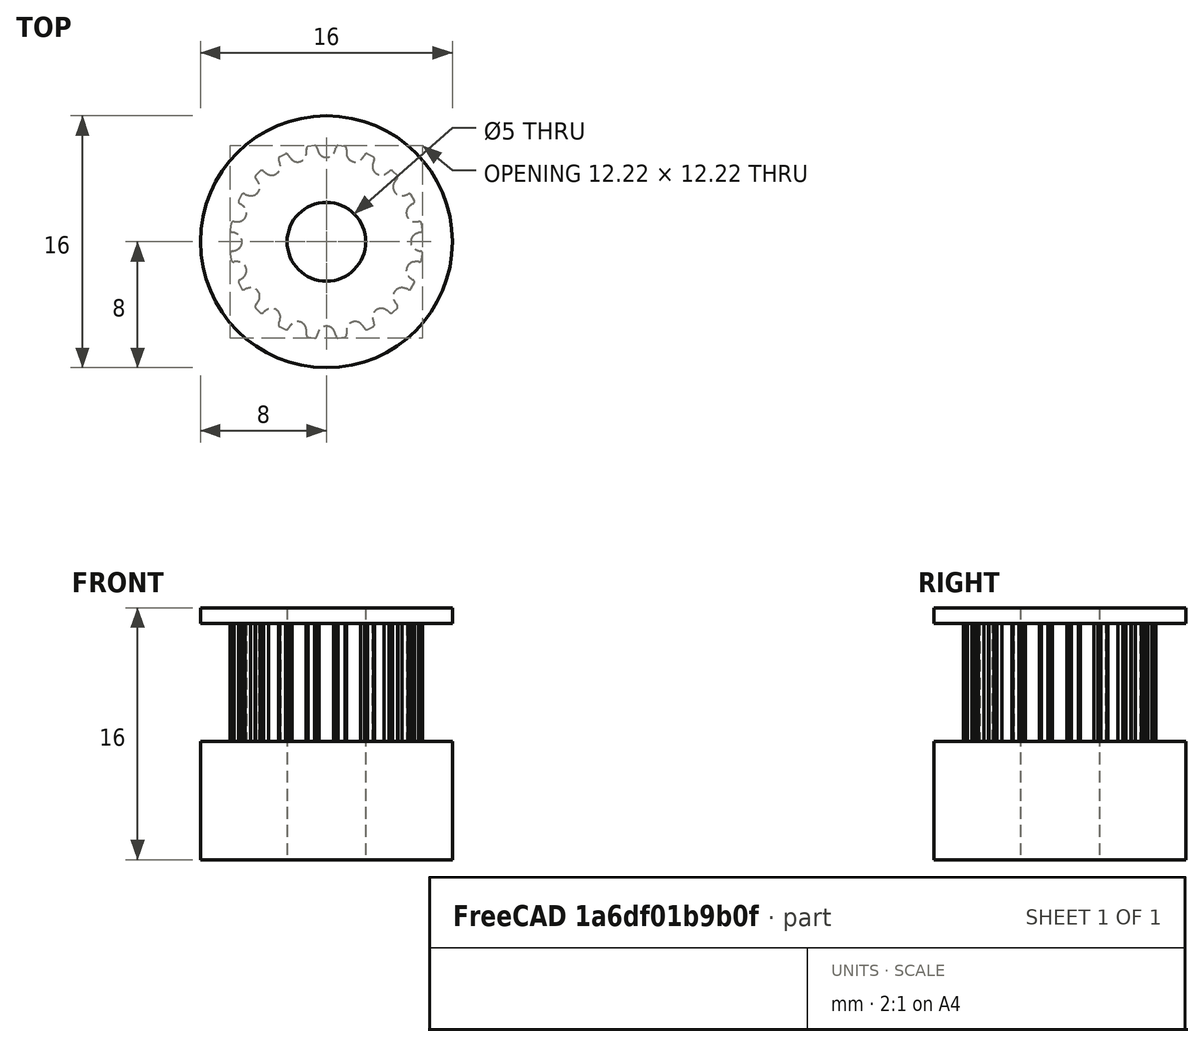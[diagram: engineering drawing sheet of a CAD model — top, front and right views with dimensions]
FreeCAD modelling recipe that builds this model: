
FCSTD DOCUMENT  (FreeCAD 1.0R39319 (Git))
Label: GT2_20
License: All rights reserved
LicenseURL: https://en.wikipedia.org/wiki/All_rights_reserved
objects: Sketcher::SketchObject×3, PartDesign::Pad×3, PartDesign::Body×1
note: 16 computed .brp shape members not serialized (recipe doc carries the construction recipe); baked Part::Feature solids carry a one-line shape summary decoded from their .brp

FEATURE [Sketcher::SketchObject] SketchGear
  ArcFitTolerance = 1e-06
  FullyConstrained = false
  MakeInternals = false
  MapMode = 5
  Placement = pos=(0,0,7.5) rot=(0,0,1;0rad)
  sketch-geometry (121):
    g0: ArcOfCircle CenterX=5.9622 CenterY=-0.75 CenterZ=0 NormalX=0 NormalY=0 NormalZ=1 AngleXU=8.1e-15 Radius=0.15 StartAngle=0 EndAngle=1.5708
    g1: ArcOfCircle CenterX=6.30816 CenterY=0.82798 CenterZ=0 NormalX=0 NormalY=0 NormalZ=-1 AngleXU=-1.3331 Radius=1.46929 StartAngle=0 EndAngle=0.255762
    g2: ArcOfCircle CenterX=5.92156 CenterY=0 CenterZ=0 NormalX=0 NormalY=0 NormalZ=-1 AngleXU=-0.984764 Radius=0.559359 StartAngle=0 EndAngle=1.96953
    g3: ArcOfCircle CenterX=6.30816 CenterY=-0.82798 CenterZ=0 NormalX=0 NormalY=0 NormalZ=-1 AngleXU=1.07734 Radius=1.46929 StartAngle=0 EndAngle=0.255762
    g4: ArcOfCircle CenterX=5.9622 CenterY=0.75 CenterZ=0 NormalX=0 NormalY=0 NormalZ=1 AngleXU=-1.5708 Radius=0.15 StartAngle=0 EndAngle=1.5708
    g5: LineSegment StartX=6.1122 StartY=0.75 StartZ=0 EndX=6.04481 EndY=1.17548 EndZ=0
    g6: ArcOfCircle CenterX=5.90215 CenterY=1.12913 CenterZ=0 NormalX=0 NormalY=0 NormalZ=1 AngleXU=0.314159 Radius=0.15 StartAngle=0 EndAngle=1.5708
    g7: ArcOfCircle CenterX=5.74356 CenterY=2.73679 CenterZ=0 NormalX=0 NormalY=0 NormalZ=-1 AngleXU=-1.64726 Radius=1.46929 StartAngle=0 EndAngle=0.255762
    g8: ArcOfCircle CenterX=5.63174 CenterY=1.82986 CenterZ=0 NormalX=0 NormalY=0 NormalZ=-1 AngleXU=-1.29892 Radius=0.559359 StartAngle=0 EndAngle=1.96953
    g9: ArcOfCircle CenterX=6.25528 CenterY=1.16187 CenterZ=0 NormalX=0 NormalY=0 NormalZ=-1 AngleXU=0.763178 Radius=1.46929 StartAngle=0 EndAngle=0.255762
    g10: ArcOfCircle CenterX=5.43862 CenterY=2.55571 CenterZ=0 NormalX=0 NormalY=0 NormalZ=1 AngleXU=-1.25664 Radius=0.15 StartAngle=0 EndAngle=1.5708
    g11: LineSegment StartX=5.58128 StartY=2.60207 StartZ=0 EndX=5.38571 EndY=2.9859 EndZ=0
    g12: ArcOfCircle CenterX=5.26436 CenterY=2.89773 CenterZ=0 NormalX=0 NormalY=0 NormalZ=1 AngleXU=0.628319 Radius=0.15 StartAngle=0 EndAngle=1.5708
    g13: ArcOfCircle CenterX=4.61674 CenterY=4.3777 CenterZ=0 NormalX=0 NormalY=0 NormalZ=-1 AngleXU=-1.96142 Radius=1.46929 StartAngle=0 EndAngle=0.255762
    g14: ArcOfCircle CenterX=4.79064 CenterY=3.4806 CenterZ=0 NormalX=0 NormalY=0 NormalZ=-1 AngleXU=-1.61308 Radius=0.559359 StartAngle=0 EndAngle=1.96953
    g15: ArcOfCircle CenterX=5.59009 CenterY=3.038 CenterZ=0 NormalX=0 NormalY=0 NormalZ=-1 AngleXU=0.449019 Radius=1.46929 StartAngle=0 EndAngle=0.255762
    g16: ArcOfCircle CenterX=4.38268 CenterY=4.11125 CenterZ=0 NormalX=0 NormalY=0 NormalZ=1 AngleXU=-0.942478 Radius=0.15 StartAngle=0 EndAngle=1.5708
    g17: LineSegment StartX=4.50403 StartY=4.19942 StartZ=0 EndX=4.19942 EndY=4.50403 EndZ=0
    g18: ArcOfCircle CenterX=4.11125 CenterY=4.38268 CenterZ=0 NormalX=0 NormalY=0 NormalZ=1 AngleXU=0.942478 Radius=0.15 StartAngle=0 EndAngle=1.5708
    g19: ArcOfCircle CenterX=3.038 CenterY=5.59009 CenterZ=0 NormalX=0 NormalY=0 NormalZ=-1 AngleXU=-2.27558 Radius=1.46929 StartAngle=0 EndAngle=0.255762
    g20: ArcOfCircle CenterX=3.4806 CenterY=4.79064 CenterZ=0 NormalX=0 NormalY=0 NormalZ=-1 AngleXU=-1.92724 Radius=0.559359 StartAngle=0 EndAngle=1.96953
    g21: ArcOfCircle CenterX=4.3777 CenterY=4.61674 CenterZ=0 NormalX=0 NormalY=0 NormalZ=-1 AngleXU=0.13486 Radius=1.46929 StartAngle=0 EndAngle=0.255762
    g22: ArcOfCircle CenterX=2.89773 CenterY=5.26436 CenterZ=0 NormalX=0 NormalY=0 NormalZ=1 AngleXU=-0.628319 Radius=0.15 StartAngle=0 EndAngle=1.5708
    g23: LineSegment StartX=2.9859 StartY=5.38571 StartZ=0 EndX=2.60207 EndY=5.58128 EndZ=0
    g24: ArcOfCircle CenterX=2.55571 CenterY=5.43862 CenterZ=0 NormalX=0 NormalY=0 NormalZ=1 AngleXU=1.25664 Radius=0.15 StartAngle=0 EndAngle=1.5708
    g25: ArcOfCircle CenterX=1.16187 CenterY=6.25528 CenterZ=0 NormalX=0 NormalY=0 NormalZ=-1 AngleXU=-2.58974 Radius=1.46929 StartAngle=0 EndAngle=0.255762
    g26: ArcOfCircle CenterX=1.82986 CenterY=5.63174 CenterZ=0 NormalX=0 NormalY=0 NormalZ=-1 AngleXU=-2.2414 Radius=0.559359 StartAngle=0 EndAngle=1.96953
    g27: ArcOfCircle CenterX=2.73679 CenterY=5.74356 CenterZ=0 NormalX=0 NormalY=0 NormalZ=-1 AngleXU=-0.1793 Radius=1.46929 StartAngle=0 EndAngle=0.255762
    g28: ArcOfCircle CenterX=1.12913 CenterY=5.90215 CenterZ=0 NormalX=0 NormalY=0 NormalZ=1 AngleXU=-0.314159 Radius=0.15 StartAngle=0 EndAngle=1.5708
    g29: LineSegment StartX=1.17548 StartY=6.04481 StartZ=0 EndX=0.75 EndY=6.1122 EndZ=0
    g30: ArcOfCircle CenterX=0.75 CenterY=5.9622 CenterZ=0 NormalX=0 NormalY=0 NormalZ=1 AngleXU=1.5708 Radius=0.15 StartAngle=0 EndAngle=1.5708
    g31: ArcOfCircle CenterX=-0.82798 CenterY=6.30816 CenterZ=0 NormalX=0 NormalY=0 NormalZ=-1 AngleXU=-2.9039 Radius=1.46929 StartAngle=0 EndAngle=0.255762
    g32: ArcOfCircle CenterX=4e-16 CenterY=5.92156 CenterZ=0 NormalX=0 NormalY=0 NormalZ=-1 AngleXU=-2.55556 Radius=0.559359 StartAngle=0 EndAngle=1.96953
    g33: ArcOfCircle CenterX=0.82798 CenterY=6.30816 CenterZ=0 NormalX=0 NormalY=0 NormalZ=-1 AngleXU=-0.493459 Radius=1.46929 StartAngle=0 EndAngle=0.255762
    g34: ArcOfCircle CenterX=-0.75 CenterY=5.9622 CenterZ=0 NormalX=0 NormalY=0 NormalZ=1 AngleXU=5.9e-15 Radius=0.15 StartAngle=0 EndAngle=1.5708
    g35: LineSegment StartX=-0.75 StartY=6.1122 StartZ=0 EndX=-1.17548 EndY=6.04481 EndZ=0
    g36: ArcOfCircle CenterX=-1.12913 CenterY=5.90215 CenterZ=0 NormalX=0 NormalY=0 NormalZ=1 AngleXU=1.88496 Radius=0.15 StartAngle=0 EndAngle=1.5708
    g37: ArcOfCircle CenterX=-2.73679 CenterY=5.74356 CenterZ=0 NormalX=0 NormalY=0 NormalZ=-1 AngleXU=3.06513 Radius=1.46929 StartAngle=0 EndAngle=0.255762
    g38: ArcOfCircle CenterX=-1.82986 CenterY=5.63174 CenterZ=0 NormalX=0 NormalY=0 NormalZ=-1 AngleXU=-2.86972 Radius=0.559359 StartAngle=0 EndAngle=1.96953
    g39: ArcOfCircle CenterX=-1.16187 CenterY=6.25528 CenterZ=0 NormalX=0 NormalY=0 NormalZ=-1 AngleXU=-0.807618 Radius=1.46929 StartAngle=0 EndAngle=0.255762
    g40: ArcOfCircle CenterX=-2.55571 CenterY=5.43862 CenterZ=0 NormalX=0 NormalY=0 NormalZ=1 AngleXU=0.314159 Radius=0.15 StartAngle=0 EndAngle=1.5708
    g41: LineSegment StartX=-2.60207 StartY=5.58128 StartZ=0 EndX=-2.9859 EndY=5.38571 EndZ=0
    g42: ArcOfCircle CenterX=-2.89773 CenterY=5.26436 CenterZ=0 NormalX=0 NormalY=0 NormalZ=1 AngleXU=2.19911 Radius=0.15 StartAngle=0 EndAngle=1.5708
    g43: ArcOfCircle CenterX=-4.3777 CenterY=4.61674 CenterZ=0 NormalX=0 NormalY=0 NormalZ=-1 AngleXU=2.75097 Radius=1.46929 StartAngle=0 EndAngle=0.255762
    g44: ArcOfCircle CenterX=-3.4806 CenterY=4.79064 CenterZ=0 NormalX=0 NormalY=0 NormalZ=-1 AngleXU=3.09931 Radius=0.559359 StartAngle=0 EndAngle=1.96953
    g45: ArcOfCircle CenterX=-3.038 CenterY=5.59009 CenterZ=0 NormalX=0 NormalY=0 NormalZ=-1 AngleXU=-1.12178 Radius=1.46929 StartAngle=0 EndAngle=0.255762
    g46: ArcOfCircle CenterX=-4.11125 CenterY=4.38268 CenterZ=0 NormalX=0 NormalY=0 NormalZ=1 AngleXU=0.628319 Radius=0.15 StartAngle=0 EndAngle=1.5708
    g47: LineSegment StartX=-4.19942 StartY=4.50403 StartZ=0 EndX=-4.50403 EndY=4.19942 EndZ=0
    g48: ArcOfCircle CenterX=-4.38268 CenterY=4.11125 CenterZ=0 NormalX=0 NormalY=0 NormalZ=1 AngleXU=2.51327 Radius=0.15 StartAngle=0 EndAngle=1.5708
    g49: ArcOfCircle CenterX=-5.59009 CenterY=3.038 CenterZ=0 NormalX=0 NormalY=0 NormalZ=-1 AngleXU=2.43681 Radius=1.46929 StartAngle=0 EndAngle=0.255762
    g50: ArcOfCircle CenterX=-4.79064 CenterY=3.4806 CenterZ=0 NormalX=0 NormalY=0 NormalZ=-1 AngleXU=2.78515 Radius=0.559359 StartAngle=0 EndAngle=1.96953
    g51: ArcOfCircle CenterX=-4.61674 CenterY=4.3777 CenterZ=0 NormalX=0 NormalY=0 NormalZ=-1 AngleXU=-1.43594 Radius=1.46929 StartAngle=0 EndAngle=0.255762
    g52: ArcOfCircle CenterX=-5.26436 CenterY=2.89773 CenterZ=0 NormalX=0 NormalY=0 NormalZ=1 AngleXU=0.942478 Radius=0.15 StartAngle=0 EndAngle=1.5708
    g53: LineSegment StartX=-5.38571 StartY=2.9859 StartZ=0 EndX=-5.58128 EndY=2.60207 EndZ=0
    g54: ArcOfCircle CenterX=-5.43862 CenterY=2.55571 CenterZ=0 NormalX=0 NormalY=0 NormalZ=1 AngleXU=2.82743 Radius=0.15 StartAngle=0 EndAngle=1.5708
    g55: ArcOfCircle CenterX=-6.25528 CenterY=1.16187 CenterZ=0 NormalX=0 NormalY=0 NormalZ=-1 AngleXU=2.12265 Radius=1.46929 StartAngle=0 EndAngle=0.255762
    g56: ArcOfCircle CenterX=-5.63174 CenterY=1.82986 CenterZ=0 NormalX=0 NormalY=0 NormalZ=-1 AngleXU=2.47099 Radius=0.559359 StartAngle=0 EndAngle=1.96953
    g57: ArcOfCircle CenterX=-5.74356 CenterY=2.73679 CenterZ=0 NormalX=0 NormalY=0 NormalZ=-1 AngleXU=-1.7501 Radius=1.46929 StartAngle=0 EndAngle=0.255762
    g58: ArcOfCircle CenterX=-5.90215 CenterY=1.12913 CenterZ=0 NormalX=0 NormalY=0 NormalZ=1 AngleXU=1.25664 Radius=0.15 StartAngle=0 EndAngle=1.5708
    g59: LineSegment StartX=-6.04481 StartY=1.17548 StartZ=0 EndX=-6.1122 EndY=0.75 EndZ=0
    g60: ArcOfCircle CenterX=-5.9622 CenterY=0.75 CenterZ=0 NormalX=0 NormalY=0 NormalZ=1 AngleXU=-3.14159 Radius=0.15 StartAngle=0 EndAngle=1.5708
    g61: ArcOfCircle CenterX=-6.30816 CenterY=-0.82798 CenterZ=0 NormalX=0 NormalY=0 NormalZ=-1 AngleXU=1.80849 Radius=1.46929 StartAngle=0 EndAngle=0.255762
    g62: ArcOfCircle CenterX=-5.92156 CenterY=9e-16 CenterZ=0 NormalX=0 NormalY=0 NormalZ=-1 AngleXU=2.15683 Radius=0.559359 StartAngle=0 EndAngle=1.96953
    g63: ArcOfCircle CenterX=-6.30816 CenterY=0.82798 CenterZ=0 NormalX=0 NormalY=0 NormalZ=-1 AngleXU=-2.06426 Radius=1.46929 StartAngle=0 EndAngle=0.255762
    g64: ArcOfCircle CenterX=-5.9622 CenterY=-0.75 CenterZ=0 NormalX=0 NormalY=0 NormalZ=1 AngleXU=1.5708 Radius=0.15 StartAngle=0 EndAngle=1.5708
    g65: LineSegment StartX=-6.1122 StartY=-0.75 StartZ=0 EndX=-6.04481 EndY=-1.17548 EndZ=0
    g66: ArcOfCircle CenterX=-5.90215 CenterY=-1.12913 CenterZ=0 NormalX=0 NormalY=0 NormalZ=1 AngleXU=-2.82743 Radius=0.15 StartAngle=0 EndAngle=1.5708
    g67: ArcOfCircle CenterX=-5.74356 CenterY=-2.73679 CenterZ=0 NormalX=0 NormalY=0 NormalZ=-1 AngleXU=1.49433 Radius=1.46929 StartAngle=0 EndAngle=0.255762
    g68: ArcOfCircle CenterX=-5.63174 CenterY=-1.82986 CenterZ=0 NormalX=0 NormalY=0 NormalZ=-1 AngleXU=1.84267 Radius=0.559359 StartAngle=0 EndAngle=1.96953
    g69: ArcOfCircle CenterX=-6.25528 CenterY=-1.16187 CenterZ=0 NormalX=0 NormalY=0 NormalZ=-1 AngleXU=-2.37841 Radius=1.46929 StartAngle=0 EndAngle=0.255762
    g70: ArcOfCircle CenterX=-5.43862 CenterY=-2.55571 CenterZ=0 NormalX=0 NormalY=0 NormalZ=1 AngleXU=1.88496 Radius=0.15 StartAngle=0 EndAngle=1.5708
    g71: LineSegment StartX=-5.58128 StartY=-2.60207 StartZ=0 EndX=-5.38571 EndY=-2.9859 EndZ=0
    g72: ArcOfCircle CenterX=-5.26436 CenterY=-2.89773 CenterZ=0 NormalX=0 NormalY=0 NormalZ=1 AngleXU=-2.51327 Radius=0.15 StartAngle=0 EndAngle=1.5708
    g73: ArcOfCircle CenterX=-4.61674 CenterY=-4.3777 CenterZ=0 NormalX=0 NormalY=0 NormalZ=-1 AngleXU=1.18017 Radius=1.46929 StartAngle=0 EndAngle=0.255762
    g74: ArcOfCircle CenterX=-4.79064 CenterY=-3.4806 CenterZ=0 NormalX=0 NormalY=0 NormalZ=-1 AngleXU=1.52851 Radius=0.559359 StartAngle=0 EndAngle=1.96953
    g75: ArcOfCircle CenterX=-5.59009 CenterY=-3.038 CenterZ=0 NormalX=0 NormalY=0 NormalZ=-1 AngleXU=-2.69257 Radius=1.46929 StartAngle=0 EndAngle=0.255762
    g76: ArcOfCircle CenterX=-4.38268 CenterY=-4.11125 CenterZ=0 NormalX=0 NormalY=0 NormalZ=1 AngleXU=2.19911 Radius=0.15 StartAngle=0 EndAngle=1.5708
    g77: LineSegment StartX=-4.50403 StartY=-4.19942 StartZ=0 EndX=-4.19942 EndY=-4.50403 EndZ=0
    g78: ArcOfCircle CenterX=-4.11125 CenterY=-4.38268 CenterZ=0 NormalX=0 NormalY=0 NormalZ=1 AngleXU=-2.19911 Radius=0.15 StartAngle=0 EndAngle=1.5708
    g79: ArcOfCircle CenterX=-3.038 CenterY=-5.59009 CenterZ=0 NormalX=0 NormalY=0 NormalZ=-1 AngleXU=0.866016 Radius=1.46929 StartAngle=0 EndAngle=0.255762
    g80: ArcOfCircle CenterX=-3.4806 CenterY=-4.79064 CenterZ=0 NormalX=0 NormalY=0 NormalZ=-1 AngleXU=1.21435 Radius=0.559359 StartAngle=0 EndAngle=1.96953
    g81: ArcOfCircle CenterX=-4.3777 CenterY=-4.61674 CenterZ=0 NormalX=0 NormalY=0 NormalZ=-1 AngleXU=-3.00673 Radius=1.46929 StartAngle=0 EndAngle=0.255762
    g82: ArcOfCircle CenterX=-2.89773 CenterY=-5.26436 CenterZ=0 NormalX=0 NormalY=0 NormalZ=1 AngleXU=2.51327 Radius=0.15 StartAngle=0 EndAngle=1.5708
    g83: LineSegment StartX=-2.9859 StartY=-5.38571 StartZ=0 EndX=-2.60207 EndY=-5.58128 EndZ=0
    g84: ArcOfCircle CenterX=-2.55571 CenterY=-5.43862 CenterZ=0 NormalX=0 NormalY=0 NormalZ=1 AngleXU=-1.88496 Radius=0.15 StartAngle=0 EndAngle=1.5708
    g85: ArcOfCircle CenterX=-1.16187 CenterY=-6.25528 CenterZ=0 NormalX=0 NormalY=0 NormalZ=-1 AngleXU=0.551856 Radius=1.46929 StartAngle=0 EndAngle=0.255762
    g86: ArcOfCircle CenterX=-1.82986 CenterY=-5.63174 CenterZ=0 NormalX=0 NormalY=0 NormalZ=-1 AngleXU=0.900192 Radius=0.559359 StartAngle=0 EndAngle=1.96953
    g87: ArcOfCircle CenterX=-2.73679 CenterY=-5.74356 CenterZ=0 NormalX=0 NormalY=0 NormalZ=-1 AngleXU=2.96229 Radius=1.46929 StartAngle=0 EndAngle=0.255762
    g88: ArcOfCircle CenterX=-1.12913 CenterY=-5.90215 CenterZ=0 NormalX=0 NormalY=0 NormalZ=1 AngleXU=2.82743 Radius=0.15 StartAngle=0 EndAngle=1.5708
    g89: LineSegment StartX=-1.17548 StartY=-6.04481 StartZ=0 EndX=-0.75 EndY=-6.1122 EndZ=0
    g90: ArcOfCircle CenterX=-0.75 CenterY=-5.9622 CenterZ=0 NormalX=0 NormalY=0 NormalZ=1 AngleXU=-1.5708 Radius=0.15 StartAngle=0 EndAngle=1.5708
    g91: ArcOfCircle CenterX=0.82798 CenterY=-6.30816 CenterZ=0 NormalX=0 NormalY=0 NormalZ=-1 AngleXU=0.237697 Radius=1.46929 StartAngle=0 EndAngle=0.255762
    g92: ArcOfCircle CenterX=-9e-16 CenterY=-5.92156 CenterZ=0 NormalX=0 NormalY=0 NormalZ=-1 AngleXU=0.586033 Radius=0.559359 StartAngle=0 EndAngle=1.96953
    g93: ArcOfCircle CenterX=-0.82798 CenterY=-6.30816 CenterZ=0 NormalX=0 NormalY=0 NormalZ=-1 AngleXU=2.64813 Radius=1.46929 StartAngle=0 EndAngle=0.255762
    g94: ArcOfCircle CenterX=0.75 CenterY=-5.9622 CenterZ=0 NormalX=0 NormalY=0 NormalZ=1 AngleXU=-3.14159 Radius=0.15 StartAngle=0 EndAngle=1.5708
    g95: LineSegment StartX=0.75 StartY=-6.1122 StartZ=0 EndX=1.17548 EndY=-6.04481 EndZ=0
    g96: ArcOfCircle CenterX=1.12913 CenterY=-5.90215 CenterZ=0 NormalX=0 NormalY=0 NormalZ=1 AngleXU=-1.25664 Radius=0.15 StartAngle=0 EndAngle=1.5708
    g97: ArcOfCircle CenterX=2.73679 CenterY=-5.74356 CenterZ=0 NormalX=0 NormalY=0 NormalZ=-1 AngleXU=-0.0764622 Radius=1.46929 StartAngle=0 EndAngle=0.255762
    g98: ArcOfCircle CenterX=1.82986 CenterY=-5.63174 CenterZ=0 NormalX=0 NormalY=0 NormalZ=-1 AngleXU=0.271874 Radius=0.559359 StartAngle=0 EndAngle=1.96953
    g99: ArcOfCircle CenterX=1.16187 CenterY=-6.25528 CenterZ=0 NormalX=0 NormalY=0 NormalZ=-1 AngleXU=2.33397 Radius=1.46929 StartAngle=0 EndAngle=0.255762
    g100: ArcOfCircle CenterX=2.55571 CenterY=-5.43862 CenterZ=0 NormalX=0 NormalY=0 NormalZ=1 AngleXU=-2.82743 Radius=0.15 StartAngle=0 EndAngle=1.5708
    g101: LineSegment StartX=2.60207 StartY=-5.58128 StartZ=0 EndX=2.9859 EndY=-5.38571 EndZ=0
    g102: ArcOfCircle CenterX=2.89773 CenterY=-5.26436 CenterZ=0 NormalX=0 NormalY=0 NormalZ=1 AngleXU=-0.942478 Radius=0.15 StartAngle=0 EndAngle=1.5708
    g103: ArcOfCircle CenterX=4.3777 CenterY=-4.61674 CenterZ=0 NormalX=0 NormalY=0 NormalZ=-1 AngleXU=-0.390621 Radius=1.46929 StartAngle=0 EndAngle=0.255762
    g104: ArcOfCircle CenterX=3.4806 CenterY=-4.79064 CenterZ=0 NormalX=0 NormalY=0 NormalZ=-1 AngleXU=-0.0422858 Radius=0.559359 StartAngle=0 EndAngle=1.96953
    g105: ArcOfCircle CenterX=3.038 CenterY=-5.59009 CenterZ=0 NormalX=0 NormalY=0 NormalZ=-1 AngleXU=2.01982 Radius=1.46929 StartAngle=0 EndAngle=0.255762
    g106: ArcOfCircle CenterX=4.11125 CenterY=-4.38268 CenterZ=0 NormalX=0 NormalY=0 NormalZ=1 AngleXU=-2.51327 Radius=0.15 StartAngle=0 EndAngle=1.5708
    g107: LineSegment StartX=4.19942 StartY=-4.50403 StartZ=0 EndX=4.50403 EndY=-4.19942 EndZ=0
    g108: ArcOfCircle CenterX=4.38268 CenterY=-4.11125 CenterZ=0 NormalX=0 NormalY=0 NormalZ=1 AngleXU=-0.628319 Radius=0.15 StartAngle=0 EndAngle=1.5708
    g109: ArcOfCircle CenterX=5.59009 CenterY=-3.038 CenterZ=0 NormalX=0 NormalY=0 NormalZ=-1 AngleXU=-0.704781 Radius=1.46929 StartAngle=0 EndAngle=0.255762
    g110: ArcOfCircle CenterX=4.79064 CenterY=-3.4806 CenterZ=0 NormalX=0 NormalY=0 NormalZ=-1 AngleXU=-0.356445 Radius=0.559359 StartAngle=0 EndAngle=1.96953
    g111: ArcOfCircle CenterX=4.61674 CenterY=-4.3777 CenterZ=0 NormalX=0 NormalY=0 NormalZ=-1 AngleXU=1.70566 Radius=1.46929 StartAngle=0 EndAngle=0.255762
    g112: ArcOfCircle CenterX=5.26436 CenterY=-2.89773 CenterZ=0 NormalX=0 NormalY=0 NormalZ=1 AngleXU=-2.19911 Radius=0.15 StartAngle=0 EndAngle=1.5708
    g113: LineSegment StartX=5.38571 StartY=-2.9859 StartZ=0 EndX=5.58128 EndY=-2.60207 EndZ=0
    g114: ArcOfCircle CenterX=5.43862 CenterY=-2.55571 CenterZ=0 NormalX=0 NormalY=0 NormalZ=1 AngleXU=-0.314159 Radius=0.15 StartAngle=0 EndAngle=1.5708
    g115: ArcOfCircle CenterX=6.25528 CenterY=-1.16187 CenterZ=0 NormalX=0 NormalY=0 NormalZ=-1 AngleXU=-1.01894 Radius=1.46929 StartAngle=0 EndAngle=0.255762
    g116: ArcOfCircle CenterX=5.63174 CenterY=-1.82986 CenterZ=0 NormalX=0 NormalY=0 NormalZ=-1 AngleXU=-0.670604 Radius=0.559359 StartAngle=0 EndAngle=1.96953
    g117: ArcOfCircle CenterX=5.74356 CenterY=-2.73679 CenterZ=0 NormalX=0 NormalY=0 NormalZ=-1 AngleXU=1.3915 Radius=1.46929 StartAngle=0 EndAngle=0.255762
    g118: ArcOfCircle CenterX=5.90215 CenterY=-1.12913 CenterZ=0 NormalX=0 NormalY=0 NormalZ=1 AngleXU=-1.88496 Radius=0.15 StartAngle=0 EndAngle=1.5708
    g119: LineSegment StartX=6.04481 StartY=-1.17548 StartZ=0 EndX=6.1122 EndY=-0.75 EndZ=0
    g120: Circle CenterX=0 CenterY=0 CenterZ=0 NormalX=0 NormalY=0 NormalZ=1 AngleXU=0 Radius=2.5
FEATURE [PartDesign::Pad] Pad
  Direction = (0,0,1)
  Length = 7.5
  Length2 = 10
  Placement = pos=(0,0,7.5) rot=(0,0,1;0rad)
  Profile = -> SketchGear
  ReferenceAxis = -> SketchGear [N_Axis]
  Refine = true
  Suppressed = false
  Type = 0
FEATURE [Sketcher::SketchObject] SketchBase
  ArcFitTolerance = 1e-06
  AttachmentOffset = pos=(0,0,-1) rot=(0,0,1;0rad)
  FullyConstrained = false
  MakeInternals = false
  MapMode = 5
  sketch-geometry (2):
    g0: Circle CenterX=0 CenterY=0 CenterZ=0 NormalX=0 NormalY=0 NormalZ=1 AngleXU=0 Radius=8
    g1: Circle CenterX=0 CenterY=0 CenterZ=0 NormalX=0 NormalY=0 NormalZ=1 AngleXU=0 Radius=2.5
  constraints (1):
    c: Diameter(g0) = 16
FEATURE [PartDesign::Pad] PadBase
  BaseFeature = -> Pad
  Direction = (0,0,1)
  Length = 7.5
  Length2 = 10
  Placement = pos=(0,0,7.5) rot=(0,0,1;0rad)
  Profile = -> SketchBase
  ReferenceAxis = -> SketchBase [N_Axis]
  Refine = true
  Suppressed = false
  Type = 0
FEATURE [Sketcher::SketchObject] SketchTop
  ArcFitTolerance = 1e-06
  AttachmentOffset = pos=(0,0,16) rot=(0,0,1;0rad)
  FullyConstrained = false
  MakeInternals = false
  MapMode = 5
  Placement = pos=(0,0,15) rot=(0,0,1;0rad)
  sketch-geometry (2):
    g0: Circle CenterX=0 CenterY=0 CenterZ=0 NormalX=0 NormalY=0 NormalZ=1 AngleXU=0 Radius=8
    g1: Circle CenterX=0 CenterY=0 CenterZ=0 NormalX=0 NormalY=0 NormalZ=1 AngleXU=0 Radius=2.5
  constraints (1):
    c: Diameter(g0) = 16
FEATURE [PartDesign::Pad] PadTop
  BaseFeature = -> PadBase
  Direction = (0,0,1)
  Length = 1
  Length2 = 10
  Placement = pos=(0,0,7.5) rot=(0,0,1;0rad)
  Profile = -> SketchTop
  ReferenceAxis = -> SketchTop [N_Axis]
  Refine = true
  Suppressed = false
  Type = 0
FEATURE [PartDesign::Body] Gear  label="GT2_Second_Min"
  AllowCompound = false
  Group = -> [SketchGear,Pad,SketchBase,PadBase,SketchTop,PadTop]
  Origin = -> Origin
  Tip = -> PadTop
